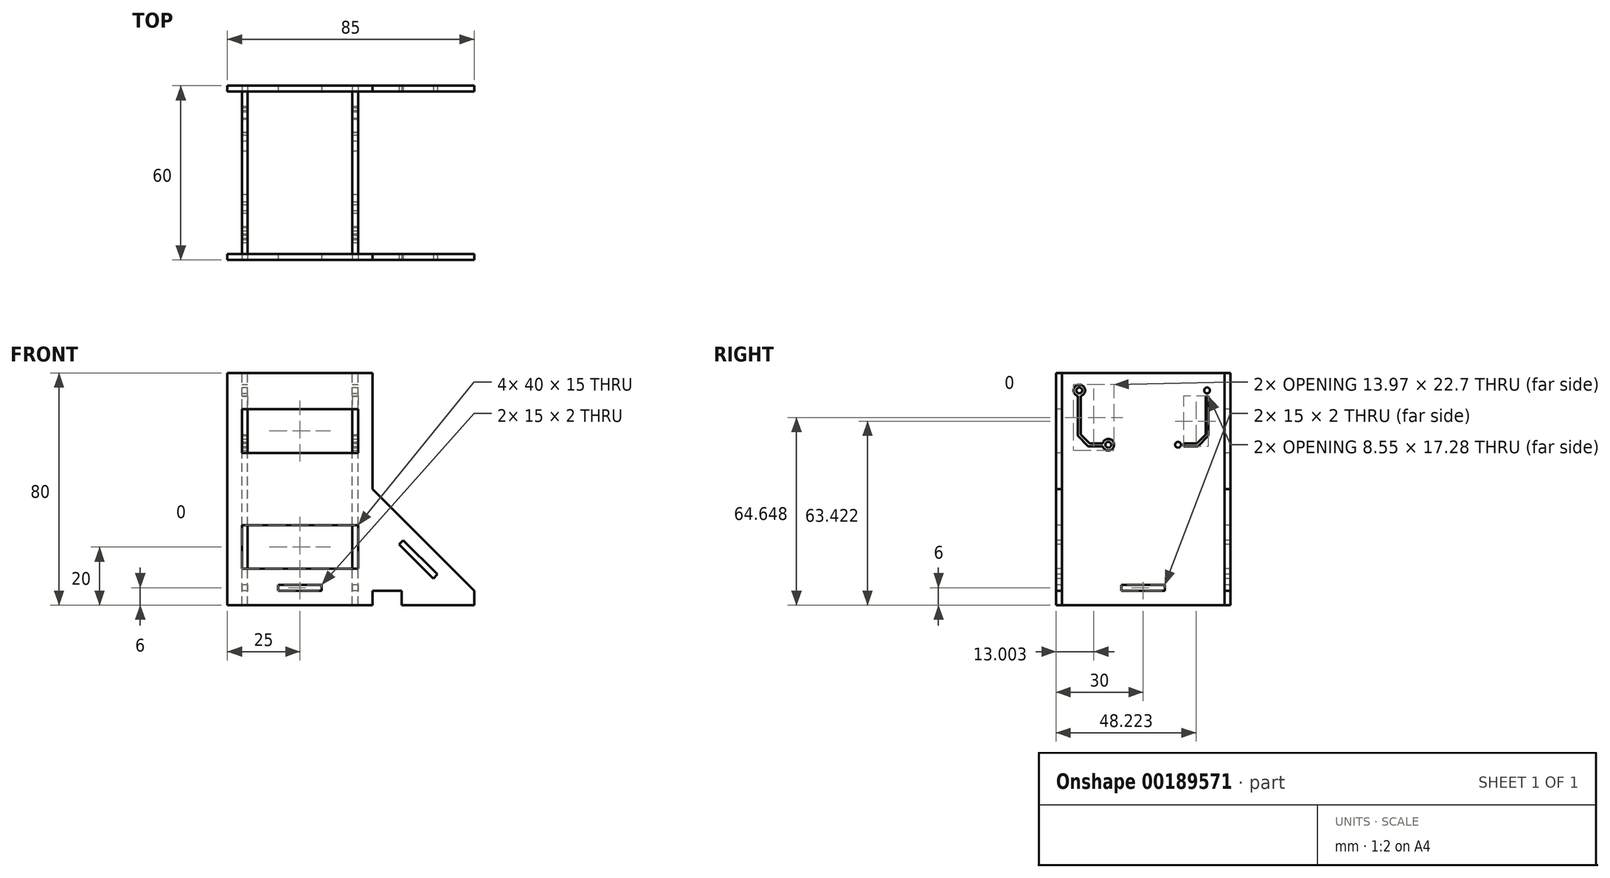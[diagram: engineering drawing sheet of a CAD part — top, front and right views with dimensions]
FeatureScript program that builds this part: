
annotation { "Feature Type Name" : "Feature", "Feature Type Description" : "" }
export const myFeature = defineFeature(function(context is Context, id is Id, definition is map)
    precondition{}
    {
        {
            var Q0;
            Q0=qCreatedBy(makeId("Front.planeOp"),FACE);
            var sketch = newSketch(context, id + "F0", { "sketchPlane" : qUnion([Q0])});
            skLineSegment(sketch, "E0.bottom", {"start": v(25, -40) * mm, "end": v(-25, -40) * mm});
            skLineSegment(sketch, "E0.top", {"start": v(25, 40) * mm, "end": v(-25, 40) * mm});
            skLineSegment(sketch, "E0.left", {"start": v(25, -40) * mm, "end": v(25, 40) * mm});
            skLineSegment(sketch, "E0.right", {"start": v(-25, -40) * mm, "end": v(-25, 40) * mm});
            skPoint(sketch, "E0.middle", {"position": v(0, 0) * mm});
            skLineSegment(sketch, "E1.bottom", {"start": v(7.5, -35) * mm, "end": v(-7.5, -35) * mm});
            skLineSegment(sketch, "E1.top", {"start": v(7.5, -33) * mm, "end": v(-7.5, -33) * mm});
            skLineSegment(sketch, "E1.left", {"start": v(7.5, -35) * mm, "end": v(7.5, -33) * mm});
            skLineSegment(sketch, "E1.right", {"start": v(-7.5, -35) * mm, "end": v(-7.5, -33) * mm});
            skPoint(sketch, "E1.middle", {"position": v(0, -34) * mm});
            skLineSegment(sketch, "E2", {"start": v(25, 0) * mm, "end": v(65, -40) * mm});
            skLineSegment(sketch, "E3", {"start": v(65, -40) * mm, "end": v(35, -40) * mm});
            skLineSegment(sketch, "E4", {"start": v(35, -40) * mm, "end": v(35, -35) * mm});
            skLineSegment(sketch, "E5", {"start": v(35, -35) * mm, "end": v(25, -35) * mm});
            skLineSegment(sketch, "E6", {"start": v(25, -7.07) * mm, "end": v(57.93, -40) * mm, "construction": true});
            skLineSegment(sketch, "E7", {"start": v(35.6, -17.68) * mm, "end": v(34.2, -19.1) * mm});
            skLineSegment(sketch, "E8", {"start": v(34.2, -19.1) * mm, "end": v(45.9, -30.8) * mm});
            skLineSegment(sketch, "E9", {"start": v(45.9, -30.8) * mm, "end": v(47.32, -29.4) * mm});
            skLineSegment(sketch, "E10", {"start": v(60, -35) * mm, "end": v(60, -40) * mm});
            skLineSegment(sketch, "E11", {"start": v(35.6, -17.68) * mm, "end": v(47.32, -29.4) * mm});
            skLineSegment(sketch, "E12", {"start": v(-20, -40) * mm, "end": v(-20, 40) * mm, "construction": true});
            skLineSegment(sketch, "E13.MirrorCS", {"start": v(20, -40) * mm, "end": v(20, 40) * mm, "construction": true});
            skLineSegment(sketch, "E14", {"start": v(-20, 27.5) * mm, "end": v(-20, 12.5) * mm});
            skLineSegment(sketch, "E15", {"start": v(-20, 12.5) * mm, "end": v(-18, 12.5) * mm});
            skLineSegment(sketch, "E16", {"start": v(-18, 12.5) * mm, "end": v(-18, 27.5) * mm});
            skLineSegment(sketch, "E17", {"start": v(-18, 27.5) * mm, "end": v(-20, 27.5) * mm});
            skLineSegment(sketch, "E18.MirrorCS", {"start": v(-18, -12.5) * mm, "end": v(-18, -27.5) * mm});
            skLineSegment(sketch, "E19.MirrorCS", {"start": v(-20, -12.5) * mm, "end": v(-18, -12.5) * mm});
            skLineSegment(sketch, "E20.MirrorCS", {"start": v(-18, -27.5) * mm, "end": v(-20, -27.5) * mm});
            skLineSegment(sketch, "E21.MirrorCS", {"start": v(20, 12.5) * mm, "end": v(18, 12.5) * mm});
            skLineSegment(sketch, "E22.MirrorCS", {"start": v(18, 12.5) * mm, "end": v(18, 27.5) * mm});
            skLineSegment(sketch, "E23.MirrorCS", {"start": v(18, 27.5) * mm, "end": v(20, 27.5) * mm});
            skLineSegment(sketch, "E24.MirrorCS", {"start": v(20, -12.5) * mm, "end": v(18, -12.5) * mm});
            skLineSegment(sketch, "E25.MirrorCS", {"start": v(18, -12.5) * mm, "end": v(18, -27.5) * mm});
            skLineSegment(sketch, "E26.MirrorCS", {"start": v(18, -27.5) * mm, "end": v(20, -27.5) * mm});
            skLineSegment(sketch, "E27", {"start": v(-20, -12.5) * mm, "end": v(-20, -27.5) * mm});
            skLineSegment(sketch, "E28", {"start": v(20, -27.5) * mm, "end": v(20, -12.5) * mm});
            skLineSegment(sketch, "E29", {"start": v(20, 12.5) * mm, "end": v(20, 27.5) * mm});
            skSolve(sketch);
        }
        {
            var Q0;
            {var subQ3=sQuery(id+"F0.wireOp",EDGE,"E0.bottom");Q0=makeQuery(id+"F0.imprint","IMPRINT",FACE,{"disambiguationData":[TD([[makeQuery(id+"F0.imprint","IMPRINT",EDGE,{"derivedFrom":subQ3}),-1.0]])]});}
            var Q1;
            {var subQ0=sQuery(id+"F0.wireOp",EDGE,"E4");Q1=makeQuery(id+"F0.imprint","IMPRINT",FACE,{"disambiguationData":[TD([[makeQuery(id+"F0.imprint","IMPRINT",EDGE,{"derivedFrom":subQ0}),-1.0]])]});}
            extrude(context, id + "F1", {"entities" : qUnion([Q0, Q1]), "endBound" : BoundingType.SYMMETRIC, "oppositeDirection" : true, "depth" : 60 * mm});
        }
        {
            var Q0;
            {var subQ3=sQuery(id+"F0.wireOp",EDGE,"E0.bottom");Q0=makeQuery(id+"F0.imprint","IMPRINT",FACE,{"disambiguationData":[TD([[makeQuery(id+"F0.imprint","IMPRINT",EDGE,{"derivedFrom":subQ3}),-1.0]])]});}
            var Q1;
            {var subQ0=sQuery(id+"F0.wireOp",EDGE,"E4");Q1=makeQuery(id+"F0.imprint","IMPRINT",FACE,{"disambiguationData":[TD([[makeQuery(id+"F0.imprint","IMPRINT",EDGE,{"derivedFrom":subQ0}),-1.0]])]});}
            extrude(context, id + "F2", {"entities" : qUnion([Q0, Q1]), "operationType" : NewBodyOperationType.REMOVE, "endBound" : BoundingType.SYMMETRIC, "oppositeDirection" : true, "depth" : 56 * mm});
        }
        {
            var Q0;
            Q0=qCreatedBy(makeId("Right.planeOp"),FACE);
            var sketch = newSketch(context, id + "F3", { "sketchPlane" : qUnion([Q0])});
            skLineSegment(sketch, "E30.0", {"start": v(30, -40) * mm, "end": v(30, 40) * mm});
            skLineSegment(sketch, "E31.0", {"start": v(-30, -40) * mm, "end": v(-30, 40) * mm});
            skLineSegment(sketch, "E32.0", {"start": v(-28, -40) * mm, "end": v(-28, 40) * mm});
            skLineSegment(sketch, "E33.0", {"start": v(28, -40) * mm, "end": v(28, 40) * mm});
            skPoint(sketch, "E34.0", {"position": v(30, 27.5) * mm});
            skPoint(sketch, "E35.0", {"position": v(30, 12.5) * mm});
            skPoint(sketch, "E36.0", {"position": v(-29, 12.5) * mm});
            skPoint(sketch, "E37.0", {"position": v(-28, 27.5) * mm});
            skPoint(sketch, "E38.0", {"position": v(30, -12.5) * mm});
            skPoint(sketch, "E39.0", {"position": v(30, -27.5) * mm});
            skPoint(sketch, "E40.0", {"position": v(-28, -27.5) * mm});
            skPoint(sketch, "E41.0", {"position": v(-28, -12.5) * mm});
            skLineSegment(sketch, "E42", {"start": v(30, 27.5) * mm, "end": v(28, 27.5) * mm});
            skLineSegment(sketch, "E43", {"start": v(30, 12.5) * mm, "end": v(28, 12.5) * mm});
            skLineSegment(sketch, "E44", {"start": v(30, -12.5) * mm, "end": v(28, -12.5) * mm});
            skLineSegment(sketch, "E45", {"start": v(30, -27.5) * mm, "end": v(28, -27.5) * mm});
            skLineSegment(sketch, "E46", {"start": v(-28, -27.5) * mm, "end": v(-30, -27.5) * mm});
            skLineSegment(sketch, "E47", {"start": v(-28, -12.5) * mm, "end": v(-30, -12.5) * mm});
            skLineSegment(sketch, "E48", {"start": v(-28, 12.5) * mm, "end": v(-30, 12.5) * mm});
            skLineSegment(sketch, "E49", {"start": v(-28, 27.5) * mm, "end": v(-30, 27.5) * mm});
            skLineSegment(sketch, "E50", {"start": v(28, 40) * mm, "end": v(-28, 40) * mm});
            skLineSegment(sketch, "E51", {"start": v(28, -40) * mm, "end": v(-28, -40) * mm});
            skPoint(sketch, "E52.0", {"position": v(30, -33) * mm});
            skPoint(sketch, "E53.0", {"position": v(30, -35) * mm});
            skPoint(sketch, "E54.0", {"position": v(-28, -33) * mm});
            skPoint(sketch, "E55.0", {"position": v(-28, -35) * mm});
            skLineSegment(sketch, "E56", {"start": v(30, -33) * mm, "end": v(28, -33) * mm});
            skLineSegment(sketch, "E57", {"start": v(-7.5, -35) * mm, "end": v(7.5, -35) * mm});
            skLineSegment(sketch, "E58", {"start": v(7.5, -33) * mm, "end": v(7.5, -35) * mm});
            skLineSegment(sketch, "E59", {"start": v(-7.5, -33) * mm, "end": v(-7.5, -35) * mm});
            skLineSegment(sketch, "E60.trimOffspring", {"start": v(7.5, -33) * mm, "end": v(-7.5, -33) * mm});
            skLineSegment(sketch, "E61.trimOffspring", {"start": v(28, -35) * mm, "end": v(30, -35) * mm});
            skSolve(sketch);
        }
        {
            var Q0;
            {var subQ7=sQuery(id+"F3.wireOp",EDGE,"E50");Q0=makeQuery(id+"F3.imprint","IMPRINT",FACE,{"disambiguationData":[TD([[makeQuery(id+"F3.imprint","IMPRINT",EDGE,{"derivedFrom":subQ7}),1.0]])]});}
            var Q1;
            {var subQ0=sQuery(id+"F3.wireOp",EDGE,"E42");Q1=makeQuery(id+"F3.imprint","IMPRINT",FACE,{"disambiguationData":[TD([[makeQuery(id+"F3.imprint","IMPRINT",EDGE,{"derivedFrom":subQ0}),1.0]])]});}
            var Q2;
            {var subQ0=sQuery(id+"F3.wireOp",EDGE,"E48");Q2=makeQuery(id+"F3.imprint","IMPRINT",FACE,{"disambiguationData":[TD([[makeQuery(id+"F3.imprint","IMPRINT",EDGE,{"derivedFrom":subQ0}),-1.0]])]});}
            var Q3;
            {var subQ0=sQuery(id+"F3.wireOp",EDGE,"E44");Q3=makeQuery(id+"F3.imprint","IMPRINT",FACE,{"disambiguationData":[TD([[makeQuery(id+"F3.imprint","IMPRINT",EDGE,{"derivedFrom":subQ0}),1.0]])]});}
            var Q4;
            {var subQ0=sQuery(id+"F3.wireOp",EDGE,"E46");Q4=makeQuery(id+"F3.imprint","IMPRINT",FACE,{"disambiguationData":[TD([[makeQuery(id+"F3.imprint","IMPRINT",EDGE,{"derivedFrom":subQ0}),-1.0]])]});}
            extrude(context, id + "F4", {"entities" : qUnion([Q0, Q1, Q2, Q3, Q4]), "endBound" : BoundingType.SYMMETRIC, "depth" : 40 * mm});
        }
        {
            var Q0;
            {var subQ7=sQuery(id+"F3.wireOp",EDGE,"E50");Q0=makeQuery(id+"F3.imprint","IMPRINT",FACE,{"disambiguationData":[TD([[makeQuery(id+"F3.imprint","IMPRINT",EDGE,{"derivedFrom":subQ7}),1.0]])]});}
            var Q1;
            {var subQ0=sQuery(id+"F3.wireOp",EDGE,"E42");Q1=makeQuery(id+"F3.imprint","IMPRINT",FACE,{"disambiguationData":[TD([[makeQuery(id+"F3.imprint","IMPRINT",EDGE,{"derivedFrom":subQ0}),1.0]])]});}
            var Q2;
            {var subQ0=sQuery(id+"F3.wireOp",EDGE,"E48");Q2=makeQuery(id+"F3.imprint","IMPRINT",FACE,{"disambiguationData":[TD([[makeQuery(id+"F3.imprint","IMPRINT",EDGE,{"derivedFrom":subQ0}),-1.0]])]});}
            var Q3;
            {var subQ0=sQuery(id+"F3.wireOp",EDGE,"E46");Q3=makeQuery(id+"F3.imprint","IMPRINT",FACE,{"disambiguationData":[TD([[makeQuery(id+"F3.imprint","IMPRINT",EDGE,{"derivedFrom":subQ0}),-1.0]])]});}
            var Q4;
            {var subQ0=sQuery(id+"F3.wireOp",EDGE,"E44");Q4=makeQuery(id+"F3.imprint","IMPRINT",FACE,{"disambiguationData":[TD([[makeQuery(id+"F3.imprint","IMPRINT",EDGE,{"derivedFrom":subQ0}),1.0]])]});}
            extrude(context, id + "F5", {"entities" : qUnion([Q0, Q1, Q2, Q3, Q4]), "operationType" : NewBodyOperationType.REMOVE, "endBound" : BoundingType.SYMMETRIC, "oppositeDirection" : true, "depth" : 36 * mm});
        }
        {
            var Q0;
            {var subQ0=sQuery(id+"F0.wireOp",EDGE,"E29");var subQ1=sQuery(id+"F0.wireOp",EDGE,"E28");var subQ2=sQuery(id+"F0.wireOp",EDGE,"E27");var subQ3=sQuery(id+"F0.wireOp",EDGE,"E26.MirrorCS");var subQ4=sQuery(id+"F0.wireOp",EDGE,"E25.MirrorCS");var subQ5=sQuery(id+"F0.wireOp",EDGE,"E24.MirrorCS");var subQ6=sQuery(id+"F0.wireOp",EDGE,"E23.MirrorCS");var subQ7=sQuery(id+"F0.wireOp",EDGE,"E22.MirrorCS");var subQ8=sQuery(id+"F0.wireOp",EDGE,"E21.MirrorCS");var subQ9=sQuery(id+"F0.wireOp",EDGE,"E20.MirrorCS");var subQ10=sQuery(id+"F0.wireOp",EDGE,"E19.MirrorCS");var subQ11=sQuery(id+"F0.wireOp",EDGE,"E18.MirrorCS");var subQ12=sQuery(id+"F0.wireOp",EDGE,"E17");var subQ13=sQuery(id+"F0.wireOp",EDGE,"E16");var subQ14=sQuery(id+"F0.wireOp",EDGE,"E15");var subQ15=sQuery(id+"F0.wireOp",EDGE,"E14");var subQ16=sQuery(id+"F0.wireOp",EDGE,"E11");var subQ17=sQuery(id+"F0.wireOp",EDGE,"E10");var subQ18=sQuery(id+"F0.wireOp",EDGE,"E9");var subQ19=sQuery(id+"F0.wireOp",EDGE,"E8");var subQ20=sQuery(id+"F0.wireOp",EDGE,"E7");var subQ21=sQuery(id+"F0.wireOp",EDGE,"E5");var subQ22=sQuery(id+"F0.wireOp",EDGE,"E4");var subQ23=sQuery(id+"F0.wireOp",EDGE,"E3");var subQ24=sQuery(id+"F0.wireOp",EDGE,"E2");var subQ25=sQuery(id+"F0.wireOp",EDGE,"E1.right");var subQ26=sQuery(id+"F0.wireOp",EDGE,"E1.left");var subQ27=sQuery(id+"F0.wireOp",EDGE,"E1.top");var subQ28=sQuery(id+"F0.wireOp",EDGE,"E1.bottom");var subQ29=sQuery(id+"F0.wireOp",EDGE,"E0.right");var subQ30=sQuery(id+"F0.wireOp",EDGE,"E0.left");var subQ31=sQuery(id+"F0.wireOp",EDGE,"E0.top");var subQ32=sQuery(id+"F0.wireOp",EDGE,"E0.bottom");Q0=makeQuery(id+"F2.boolean.opBoolean","SPLIT",FACE,{"disambiguationData":[TD([makeQuery(id+"F1.opExtrude","CAP_FACE",FACE,{"disambiguationData":[OSD([subQ32,subQ31,subQ30,subQ29,subQ28,subQ27,subQ26,subQ25,subQ24,subQ23,subQ22,subQ21,subQ20,subQ19,subQ18,subQ17,subQ16,subQ15,subQ14,subQ13,subQ12,subQ11,subQ10,subQ9,subQ8,subQ7,subQ6,subQ5,subQ4,subQ3,subQ2,subQ1,subQ0])],"isStart":false})])],"derivedFrom":makeQuery(id+"F1.opExtrude","SWEPT_FACE",FACE,{"disambiguationData":[OSD([subQ19])]})});}
            var sketch = newSketch(context, id + "F6", { "sketchPlane" : qUnion([Q0])});
            skLineSegment(sketch, "E62.0", {"start": v(-28, -17.68) * mm, "end": v(-28, -67.18) * mm});
            skLineSegment(sketch, "E63.0", {"start": v(-30, -17.68) * mm, "end": v(-30, -67.18) * mm});
            skLineSegment(sketch, "E64.0", {"start": v(28, -17.68) * mm, "end": v(28, -67.18) * mm});
            skLineSegment(sketch, "E65.0", {"start": v(30, -17.68) * mm, "end": v(30, -67.18) * mm});
            skLineSegment(sketch, "E66.0.0", {"start": v(-28, -54.25) * mm, "end": v(-28, -37.68) * mm});
            skLineSegment(sketch, "E66.0.1", {"start": v(-28, -37.68) * mm, "end": v(-30, -37.68) * mm});
            skLineSegment(sketch, "E66.0.2", {"start": v(-30, -37.68) * mm, "end": v(-30, -54.25) * mm});
            skLineSegment(sketch, "E66.0.3", {"start": v(-30, -54.25) * mm, "end": v(-28, -54.25) * mm});
            skLineSegment(sketch, "E67.0.0", {"start": v(30, -37.68) * mm, "end": v(28, -37.68) * mm});
            skLineSegment(sketch, "E67.0.1", {"start": v(28, -37.68) * mm, "end": v(28, -54.25) * mm});
            skLineSegment(sketch, "E67.0.2", {"start": v(28, -54.25) * mm, "end": v(30, -54.25) * mm});
            skLineSegment(sketch, "E67.0.3", {"start": v(30, -54.25) * mm, "end": v(30, -37.68) * mm});
            skLineSegment(sketch, "E68", {"start": v(-28, -17.68) * mm, "end": v(28, -17.68) * mm});
            skLineSegment(sketch, "E69", {"start": v(28, -67.18) * mm, "end": v(-28, -67.18) * mm});
            skSolve(sketch);
        }
        {
            var Q0;
            Q0=makeQuery(id+"F6.imprint","IMPRINT",FACE,{"disambiguationData":[TD([[makeQuery(id+"F6.imprint","IMPRINT",EDGE,{"derivedFrom":sQuery(id+"F6.wireOp",EDGE,"E66.0.0")}),1.0]])]});
            var Q1;
            {var subQ5=sQuery(id+"F6.wireOp",EDGE,"E66.0.0");Q1=makeQuery(id+"F6.imprint","IMPRINT",FACE,{"disambiguationData":[TD([[makeQuery(id+"F6.imprint","IMPRINT",EDGE,{"derivedFrom":subQ5}),-1.0]])]});}
            var Q2;
            Q2=makeQuery(id+"F6.imprint","IMPRINT",FACE,{"disambiguationData":[TD([[makeQuery(id+"F6.imprint","IMPRINT",EDGE,{"derivedFrom":sQuery(id+"F6.wireOp",EDGE,"E67.0.0")}),1.0]])]});
            extrude(context, id + "F7", {"entities" : qUnion([Q0, Q1, Q2]), "depth" : 2 * mm});
        }
        {
            var Q0;
            Q0=makeQuery(id+"F4.opExtrude","CAP_FACE",FACE,{"disambiguationData":[OSD([sQuery(id+"F3.wireOp",EDGE,"E30.0"),sQuery(id+"F3.wireOp",EDGE,"E31.0"),sQuery(id+"F3.wireOp",EDGE,"E32.0"),sQuery(id+"F3.wireOp",EDGE,"E33.0"),sQuery(id+"F3.wireOp",EDGE,"E42"),sQuery(id+"F3.wireOp",EDGE,"E43"),sQuery(id+"F3.wireOp",EDGE,"E44"),sQuery(id+"F3.wireOp",EDGE,"E45"),sQuery(id+"F3.wireOp",EDGE,"E46"),sQuery(id+"F3.wireOp",EDGE,"E47"),sQuery(id+"F3.wireOp",EDGE,"E48"),sQuery(id+"F3.wireOp",EDGE,"E49"),sQuery(id+"F3.wireOp",EDGE,"E50"),sQuery(id+"F3.wireOp",EDGE,"E51"),sQuery(id+"F3.wireOp",EDGE,"E57"),sQuery(id+"F3.wireOp",EDGE,"E58"),sQuery(id+"F3.wireOp",EDGE,"E59"),sQuery(id+"F3.wireOp",EDGE,"E60.trimOffspring")])],"isStart":false});
            var sketch = newSketch(context, id + "F8", { "sketchPlane" : qUnion([Q0])});
            skCircle(sketch, "E70", {"center": v(-22, 34) * mm, "radius": 2 * mm});
            skCircle(sketch, "E71", {"center": v(-22, 34) * mm, "radius": 1 * mm});
            skLineSegment(sketch, "E72", {"start": v(-22, 34) * mm, "end": v(-22, 0) * mm, "construction": true});
            skLineSegment(sketch, "E73", {"start": v(-21.5, 33.83) * mm, "end": v(-21.5, 18.8) * mm});
            skLineSegment(sketch, "E74.MirrorCS", {"start": v(-22.5, 33.83) * mm, "end": v(-22.5, 18.8) * mm});
            skLineSegment(sketch, "E75", {"start": v(-18.48, 14.78) * mm, "end": v(-12, 14.78) * mm});
            skLineSegment(sketch, "E76", {"start": v(-18.48, 15.78) * mm, "end": v(-12, 15.78) * mm});
            skLineSegment(sketch, "E77", {"start": v(-21.5, 18.8) * mm, "end": v(-18.48, 15.78) * mm});
            skLineSegment(sketch, "E78", {"start": v(-22.5, 18.39) * mm, "end": v(-18.9, 14.78) * mm});
            skLineSegment(sketch, "E79", {"start": v(-22.5, 18.8) * mm, "end": v(-22.5, 18.39) * mm});
            skLineSegment(sketch, "E80", {"start": v(-18.48, 14.78) * mm, "end": v(-18.9, 14.78) * mm});
            skLineSegment(sketch, "E81", {"start": v(-12, 14.78) * mm, "end": v(-12, 15.78) * mm, "construction": true});
            skLineSegment(sketch, "E82", {"start": v(-12, 15.28) * mm, "end": v(-18.48, 15.28) * mm, "construction": true});
            skCircle(sketch, "E83", {"center": v(-12, 15.28) * mm, "radius": 1 * mm});
            skCircle(sketch, "E84", {"center": v(-12, 15.28) * mm, "radius": 2 * mm});
            skCircle(sketch, "E85.MirrorC", {"center": v(12, 15.28) * mm, "radius": 1 * mm});
            skLineSegment(sketch, "E86.MirrorCS", {"start": v(12, 14.78) * mm, "end": v(12, 15.78) * mm, "construction": true});
            skLineSegment(sketch, "E87.MirrorCS", {"start": v(22.5, 18.8) * mm, "end": v(22.5, 18.39) * mm});
            skLineSegment(sketch, "E88.MirrorCS", {"start": v(18.48, 14.78) * mm, "end": v(18.9, 14.78) * mm});
            skCircle(sketch, "E89.MirrorC", {"center": v(22, 34) * mm, "radius": 1 * mm});
            skLineSegment(sketch, "E90.MirrorCS", {"start": v(22.5, 18.39) * mm, "end": v(18.9, 14.78) * mm});
            skLineSegment(sketch, "E91.MirrorCS", {"start": v(21.5, 18.8) * mm, "end": v(18.48, 15.78) * mm});
            skLineSegment(sketch, "E92.MirrorCS", {"start": v(21.5, 33.83) * mm, "end": v(21.5, 18.8) * mm});
            skLineSegment(sketch, "E93.MirrorCS", {"start": v(22.5, 33.83) * mm, "end": v(22.5, 18.8) * mm});
            skCircle(sketch, "E94.MirrorC", {"center": v(22, 34) * mm, "radius": 2 * mm});
            skCircle(sketch, "E95.MirrorC", {"center": v(12, 15.28) * mm, "radius": 2 * mm});
            skLineSegment(sketch, "E96.MirrorCS", {"start": v(12, 15.28) * mm, "end": v(18.48, 15.28) * mm, "construction": true});
            skLineSegment(sketch, "E97.MirrorCS", {"start": v(18.48, 15.78) * mm, "end": v(12, 15.78) * mm});
            skLineSegment(sketch, "E98.MirrorCS", {"start": v(18.48, 14.78) * mm, "end": v(12, 14.78) * mm});
            skSolve(sketch);
        }
        {
            var Q0;
            {var subQ10=sQuery(id+"F8.wireOp",EDGE,"E77");Q0=makeQuery(id+"F8.imprint","IMPRINT",FACE,{"disambiguationData":[TD([[makeQuery(id+"F8.imprint","IMPRINT",EDGE,{"derivedFrom":subQ10}),-1.0]])]});}
            var Q1;
            {var subQ0=sQuery(id+"F8.wireOp",EDGE,"E83");var subQ1=sQuery(id+"F8.wireOp",EDGE,"E75");var subQ2=makeQuery(id+"F8.imprint","INTERSECT",VERTEX,{"derivedFrom":[subQ1,subQ0]});Q1=makeQuery(id+"F8.imprint","IMPRINT",FACE,{"disambiguationData":[TD([[makeQuery(id+"F8.imprint","IMPRINT",EDGE,{"disambiguationData":[TD([[subQ2,1.0]])],"derivedFrom":subQ1}),-1.0]])]});}
            var Q2;
            {var subQ0=sQuery(id+"F8.wireOp",EDGE,"E83");var subQ1=sQuery(id+"F8.wireOp",EDGE,"E75");var subQ2=makeQuery(id+"F8.imprint","INTERSECT",VERTEX,{"derivedFrom":[subQ1,subQ0]});Q2=makeQuery(id+"F8.imprint","IMPRINT",FACE,{"disambiguationData":[TD([[makeQuery(id+"F8.imprint","IMPRINT",EDGE,{"disambiguationData":[TD([[subQ2,1.0]])],"derivedFrom":subQ1}),1.0]])]});}
            var Q3;
            {var subQ0=sQuery(id+"F8.wireOp",EDGE,"E73");var subQ1=sQuery(id+"F8.wireOp",EDGE,"E70");var subQ2=makeQuery(id+"F8.imprint","INTERSECT",VERTEX,{"derivedFrom":[subQ1,subQ0]});Q3=makeQuery(id+"F8.imprint","IMPRINT",FACE,{"disambiguationData":[TD([[makeQuery(id+"F8.imprint","IMPRINT",EDGE,{"disambiguationData":[TD([[subQ2,-1.0]])],"derivedFrom":subQ1}),1.0]])]});}
            var Q4;
            {var subQ0=sQuery(id+"F8.wireOp",EDGE,"E73");var subQ1=sQuery(id+"F8.wireOp",EDGE,"E70");var subQ2=makeQuery(id+"F8.imprint","INTERSECT",VERTEX,{"derivedFrom":[subQ1,subQ0]});Q4=makeQuery(id+"F8.imprint","IMPRINT",FACE,{"disambiguationData":[TD([[makeQuery(id+"F8.imprint","IMPRINT",EDGE,{"disambiguationData":[TD([[subQ2,1.0]])],"derivedFrom":subQ1}),1.0]])]});}
            var Q5;
            {var subQ0=sQuery(id+"F8.wireOp",EDGE,"E92.MirrorCS");var subQ1=sQuery(id+"F8.wireOp",EDGE,"E89.MirrorC");var subQ2=makeQuery(id+"F8.imprint","INTERSECT",VERTEX,{"derivedFrom":[subQ1,subQ0]});Q5=makeQuery(id+"F8.imprint","IMPRINT",FACE,{"disambiguationData":[TD([[makeQuery(id+"F8.imprint","IMPRINT",EDGE,{"disambiguationData":[TD([[subQ2,-1.0]])],"derivedFrom":subQ1}),1.0]])]});}
            var Q6;
            {var subQ0=sQuery(id+"F8.wireOp",EDGE,"E92.MirrorCS");var subQ1=sQuery(id+"F8.wireOp",EDGE,"E89.MirrorC");var subQ2=makeQuery(id+"F8.imprint","INTERSECT",VERTEX,{"derivedFrom":[subQ1,subQ0]});Q6=makeQuery(id+"F8.imprint","IMPRINT",FACE,{"disambiguationData":[TD([[makeQuery(id+"F8.imprint","IMPRINT",EDGE,{"disambiguationData":[TD([[subQ2,1.0]])],"derivedFrom":subQ1}),1.0]])]});}
            var Q7;
            {var subQ10=sQuery(id+"F8.wireOp",EDGE,"E87.MirrorCS");Q7=makeQuery(id+"F8.imprint","IMPRINT",FACE,{"disambiguationData":[TD([[makeQuery(id+"F8.imprint","IMPRINT",EDGE,{"derivedFrom":subQ10}),-1.0]])]});}
            var Q8;
            {var subQ0=sQuery(id+"F8.wireOp",EDGE,"E97.MirrorCS");var subQ1=sQuery(id+"F8.wireOp",EDGE,"E85.MirrorC");var subQ2=makeQuery(id+"F8.imprint","INTERSECT",VERTEX,{"derivedFrom":[subQ1,subQ0]});Q8=makeQuery(id+"F8.imprint","IMPRINT",FACE,{"disambiguationData":[TD([[makeQuery(id+"F8.imprint","IMPRINT",EDGE,{"disambiguationData":[TD([[subQ2,-1.0]])],"derivedFrom":subQ1}),1.0]])]});}
            var Q9;
            {var subQ0=sQuery(id+"F8.wireOp",EDGE,"E97.MirrorCS");var subQ1=sQuery(id+"F8.wireOp",EDGE,"E85.MirrorC");var subQ2=makeQuery(id+"F8.imprint","INTERSECT",VERTEX,{"derivedFrom":[subQ1,subQ0]});Q9=makeQuery(id+"F8.imprint","IMPRINT",FACE,{"disambiguationData":[TD([[makeQuery(id+"F8.imprint","IMPRINT",EDGE,{"disambiguationData":[TD([[subQ2,1.0]])],"derivedFrom":subQ1}),1.0]])]});}
            var Q10;
            Q10=makeQuery(id+"F4.opExtrude","CAP_FACE",FACE,{"disambiguationData":[OSD([sQuery(id+"F3.wireOp",EDGE,"E30.0"),sQuery(id+"F3.wireOp",EDGE,"E31.0"),sQuery(id+"F3.wireOp",EDGE,"E32.0"),sQuery(id+"F3.wireOp",EDGE,"E33.0"),sQuery(id+"F3.wireOp",EDGE,"E42"),sQuery(id+"F3.wireOp",EDGE,"E43"),sQuery(id+"F3.wireOp",EDGE,"E44"),sQuery(id+"F3.wireOp",EDGE,"E45"),sQuery(id+"F3.wireOp",EDGE,"E46"),sQuery(id+"F3.wireOp",EDGE,"E47"),sQuery(id+"F3.wireOp",EDGE,"E48"),sQuery(id+"F3.wireOp",EDGE,"E49"),sQuery(id+"F3.wireOp",EDGE,"E50"),sQuery(id+"F3.wireOp",EDGE,"E51"),sQuery(id+"F3.wireOp",EDGE,"E57"),sQuery(id+"F3.wireOp",EDGE,"E58"),sQuery(id+"F3.wireOp",EDGE,"E59"),sQuery(id+"F3.wireOp",EDGE,"E60.trimOffspring")])],"isStart":true});
            extrude(context, id + "F9", {"entities" : qUnion([Q0, Q1, Q2, Q3, Q4, Q5, Q6, Q7, Q8, Q9]), "operationType" : NewBodyOperationType.REMOVE, "endBound" : BoundingType.UP_TO_SURFACE, "oppositeDirection" : true, "endBoundEntityFace" : qUnion([Q10]), "depth" : 80 * mm});
        }
    });
